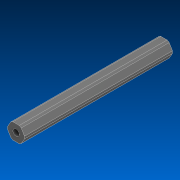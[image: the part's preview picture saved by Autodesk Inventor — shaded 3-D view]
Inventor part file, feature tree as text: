
AUTODESK INVENTOR PART (.ipt)
format: ipt  version: 2022.2 (Build 262287000, 287)  size: 122,880 bytes
history: native  units: in
note: dims shown in document units (in); Inventor stores cm internally (conversion verified against a paired STEP export)
features: extrude x1, sketch x1, other x1
ambient origin geometry x8: Origin, YZ Plane, XZ Plane, XY Plane, X Axis, Y Axis, Z Axis, Center Point
bodies: Solid1 (feature_tree)
feature tree (3):
  extrude  "Extrusion1"  TaperAngle=0.0deg  [1 undecoded]
  sketch  "Sketch1"  dims[d0=31.3in d1=0.0in]
  other  "Cut-Extrude2"
note: 1 required parameter value undecoded (feature->parameter linkage not recoverable at this tier; creation-order binding heuristic only, values carry confidence <= 0.55)
